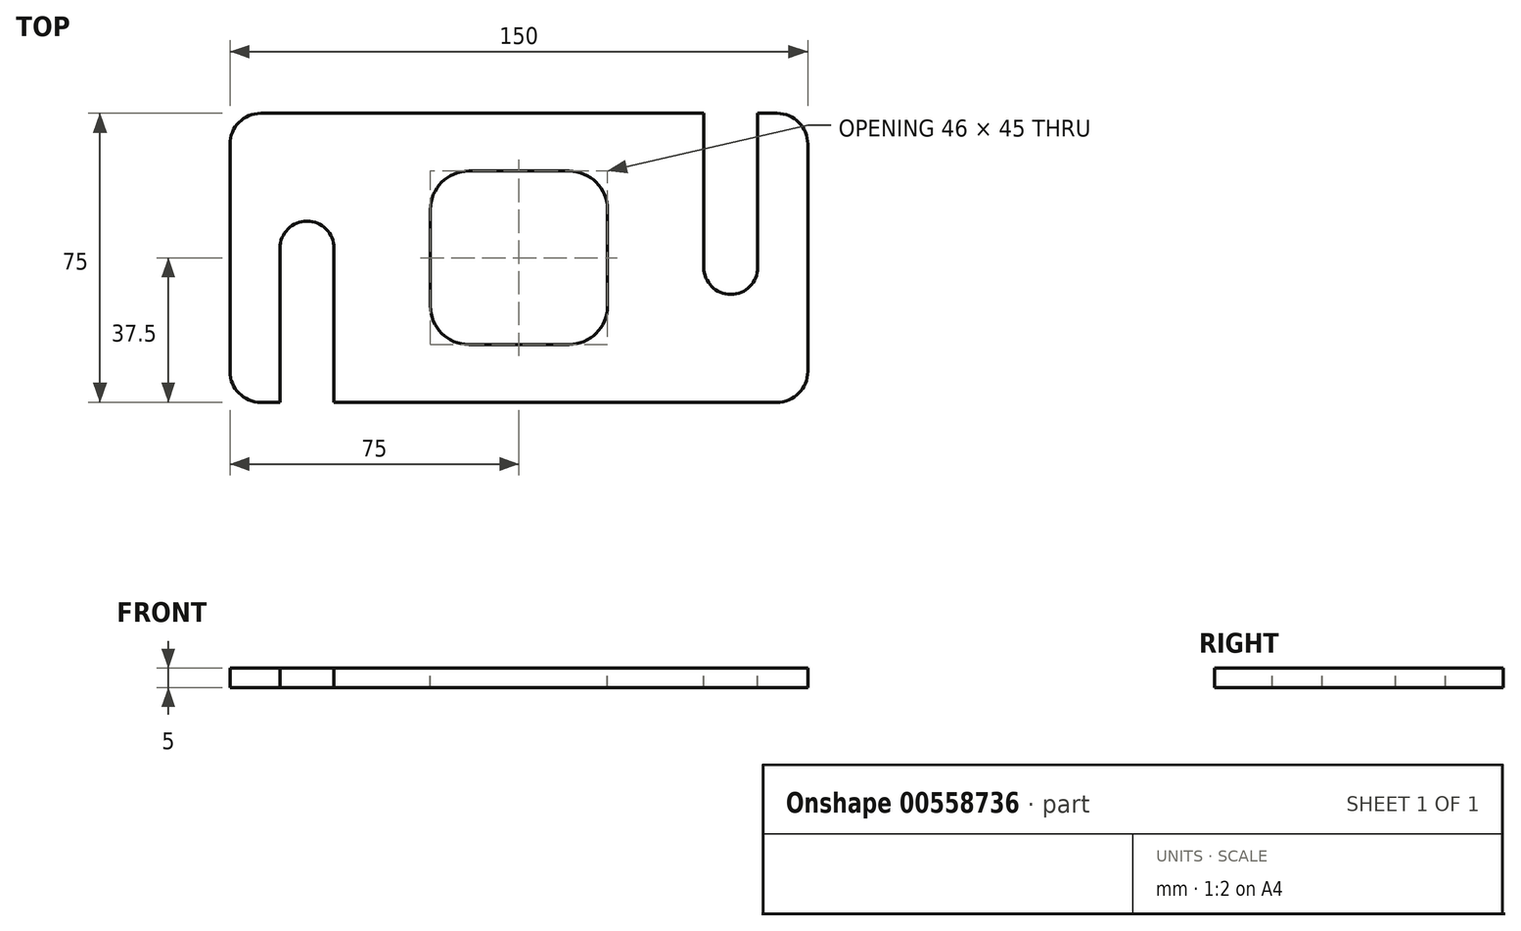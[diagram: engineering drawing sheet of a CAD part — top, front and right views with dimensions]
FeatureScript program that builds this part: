
annotation { "Feature Type Name" : "Feature", "Feature Type Description" : "" }
export const myFeature = defineFeature(function(context is Context, id is Id, definition is map)
    precondition{}
    {
        {
            var Q0;
            Q0=qCreatedBy(makeId("Top.planeOp"),FACE);
            var sketch = newSketch(context, id + "F0", { "sketchPlane" : qUnion([Q0])});
            skLineSegment(sketch, "E0.bottom", {"start": v(0, 0) * mm, "end": v(150, 0) * mm});
            skLineSegment(sketch, "E0.top", {"start": v(0, 75) * mm, "end": v(150, 75) * mm});
            skLineSegment(sketch, "E0.left", {"start": v(0, 0) * mm, "end": v(0, 75) * mm});
            skLineSegment(sketch, "E0.right", {"start": v(150, 0) * mm, "end": v(150, 75) * mm});
            skSolve(sketch);
        }
        {
            var Q0;
            Q0=qSketchRegion(id+"F0",true);
            extrude(context, id + "F1", {"entities" : qUnion([Q0]), "depth" : 5 * mm, "offsetDistance" : 25 * mm});
        }
        {
            var Q0;
            Q0=makeQuery(id+"F1.opExtrude","CAP_FACE",FACE,{"disambiguationData":[OSD([sQuery(id+"F0.wireOp",EDGE,"E0.bottom"),sQuery(id+"F0.wireOp",EDGE,"E0.top"),sQuery(id+"F0.wireOp",EDGE,"E0.left"),sQuery(id+"F0.wireOp",EDGE,"E0.right")])],"isStart":false});
            var sketch = newSketch(context, id + "F2", { "sketchPlane" : qUnion([Q0])});
            skLineSegment(sketch, "E1", {"start": v(13, 0) * mm, "end": v(27, 0) * mm});
            skLineSegment(sketch, "E2", {"start": v(27, 0) * mm, "end": v(27, 40) * mm});
            skLineSegment(sketch, "E3", {"start": v(13, 0) * mm, "end": v(13, 40) * mm});
            skLineSegment(sketch, "E4", {"start": v(123, 35) * mm, "end": v(123, 75) * mm});
            skLineSegment(sketch, "E5", {"start": v(123, 75) * mm, "end": v(137, 75) * mm});
            skLineSegment(sketch, "E6", {"start": v(137, 75) * mm, "end": v(137, 35) * mm});
            skArc(sketch, "E7", {"start": v(13, 40) * mm, "mid": v(20, 47) * mm, "end": v(27, 40) * mm});
            skArc(sketch, "E8", {"start": v(123, 35) * mm, "mid": v(130, 28) * mm, "end": v(137, 35) * mm});
            skSolve(sketch);
        }
        {
            var Q0;
            Q0=qSketchRegion(id+"F2",true);
            extrude(context, id + "F3", {"entities" : qUnion([Q0]), "operationType" : NewBodyOperationType.REMOVE, "endBound" : BoundingType.THROUGH_ALL, "oppositeDirection" : true, "depth" : 25 * mm, "offsetDistance" : 25 * mm});
        }
        {
            var Q0;
            Q0=makeQuery(id+"F1.opExtrude","CAP_FACE",FACE,{"disambiguationData":[OSD([sQuery(id+"F0.wireOp",EDGE,"E0.bottom"),sQuery(id+"F0.wireOp",EDGE,"E0.top"),sQuery(id+"F0.wireOp",EDGE,"E0.left"),sQuery(id+"F0.wireOp",EDGE,"E0.right")])],"isStart":false});
            var sketch = newSketch(context, id + "F4", { "sketchPlane" : qUnion([Q0])});
            skLineSegment(sketch, "E9.bottom", {"start": v(52, 15) * mm, "end": v(98, 15) * mm});
            skLineSegment(sketch, "E9.top", {"start": v(52, 60) * mm, "end": v(98, 60) * mm});
            skLineSegment(sketch, "E9.left", {"start": v(52, 15) * mm, "end": v(52, 60) * mm});
            skLineSegment(sketch, "E9.right", {"start": v(98, 15) * mm, "end": v(98, 60) * mm});
            skSolve(sketch);
        }
        {
            var Q0;
            Q0=qSketchRegion(id+"F4",true);
            extrude(context, id + "F5", {"entities" : qUnion([Q0]), "operationType" : NewBodyOperationType.REMOVE, "endBound" : BoundingType.THROUGH_ALL, "oppositeDirection" : true, "depth" : 25 * mm, "offsetDistance" : 25 * mm});
        }
        {
            var Q0;
            Q0=makeQuery(id+"F5.boolean.opBoolean","COPY",EDGE,{"derivedFrom":makeQuery(id+"F5.opExtrude","SWEPT_EDGE",EDGE,{"disambiguationData":[OSD([sQuery(id+"F4.wireOp",EDGE,"E9.top"),sQuery(id+"F4.wireOp",EDGE,"E9.left")])]})});
            var Q1;
            Q1=makeQuery(id+"F5.boolean.opBoolean","COPY",EDGE,{"derivedFrom":makeQuery(id+"F5.opExtrude","SWEPT_EDGE",EDGE,{"disambiguationData":[OSD([sQuery(id+"F4.wireOp",EDGE,"E9.top"),sQuery(id+"F4.wireOp",EDGE,"E9.right")])]})});
            var Q2;
            Q2=makeQuery(id+"F5.boolean.opBoolean","COPY",EDGE,{"derivedFrom":makeQuery(id+"F5.opExtrude","SWEPT_EDGE",EDGE,{"disambiguationData":[OSD([sQuery(id+"F4.wireOp",EDGE,"E9.bottom"),sQuery(id+"F4.wireOp",EDGE,"E9.right")])]})});
            var Q3;
            Q3=makeQuery(id+"F5.boolean.opBoolean","COPY",EDGE,{"derivedFrom":makeQuery(id+"F5.opExtrude","SWEPT_EDGE",EDGE,{"disambiguationData":[OSD([sQuery(id+"F4.wireOp",EDGE,"E9.bottom"),sQuery(id+"F4.wireOp",EDGE,"E9.left")])]})});
            fillet(context, id + "F6", {"entities" : qUnion([Q0, Q1, Q2, Q3]), "radius" : 10 * mm, "tangentPropagation" : true, "allowEdgeOverflow" : false});
        }
        {
            var Q0;
            Q0=makeQuery(id+"F1.opExtrude","SWEPT_EDGE",EDGE,{"disambiguationData":[OSD([sQuery(id+"F0.wireOp",EDGE,"E0.top"),sQuery(id+"F0.wireOp",EDGE,"E0.left")])]});
            var Q1;
            Q1=makeQuery(id+"F1.opExtrude","SWEPT_EDGE",EDGE,{"disambiguationData":[OSD([sQuery(id+"F0.wireOp",EDGE,"E0.top"),sQuery(id+"F0.wireOp",EDGE,"E0.right")])]});
            var Q2;
            Q2=makeQuery(id+"F1.opExtrude","SWEPT_EDGE",EDGE,{"disambiguationData":[OSD([sQuery(id+"F0.wireOp",EDGE,"E0.bottom"),sQuery(id+"F0.wireOp",EDGE,"E0.right")])]});
            var Q3;
            Q3=makeQuery(id+"F1.opExtrude","SWEPT_EDGE",EDGE,{"disambiguationData":[OSD([sQuery(id+"F0.wireOp",EDGE,"E0.bottom"),sQuery(id+"F0.wireOp",EDGE,"E0.left")])]});
            fillet(context, id + "F7", {"entities" : qUnion([Q0, Q1, Q2, Q3]), "radius" : 8 * mm, "tangentPropagation" : true, "allowEdgeOverflow" : false});
        }
    });
